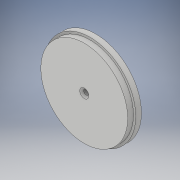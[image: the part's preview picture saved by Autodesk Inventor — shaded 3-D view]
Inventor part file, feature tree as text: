
AUTODESK INVENTOR PART (.ipt)
format: ipt  version: 2019 (Build 230136000, 136)  size: 259,584 bytes
history: native  units: mm
features: sketch x4, extrude x3, projected_geometry x2, other x1, hole x1
ambient origin geometry x8: Origin, YZ Plane, XZ Plane, XY Plane, X Axis, Y Axis, Z Axis, Center Point
bodies: Body1 (feature_tree)
feature tree (11):
  other  "Твердое тело1"
  extrude  "Выдавливание1"  Depth=80.0mm
  extrude  "Выдавливание2"  Depth=5.0mm TaperAngle=0.0deg
  extrude  "Выдавливание3"  Depth=4.0mm TaperAngle=0.0deg
  hole  "Отверстие1"  [1 undecoded]
  sketch  "Эскиз1"
  sketch  "Эскиз2"
  sketch  "Эскиз3"
  projected_geometry  "Спроецированная петля1"
  sketch  "Эскиз5"
  projected_geometry  "Спроецированная петля2"
note: 1 required parameter value undecoded (feature->parameter linkage not recoverable at this tier; creation-order binding heuristic only, values carry confidence <= 0.55)
